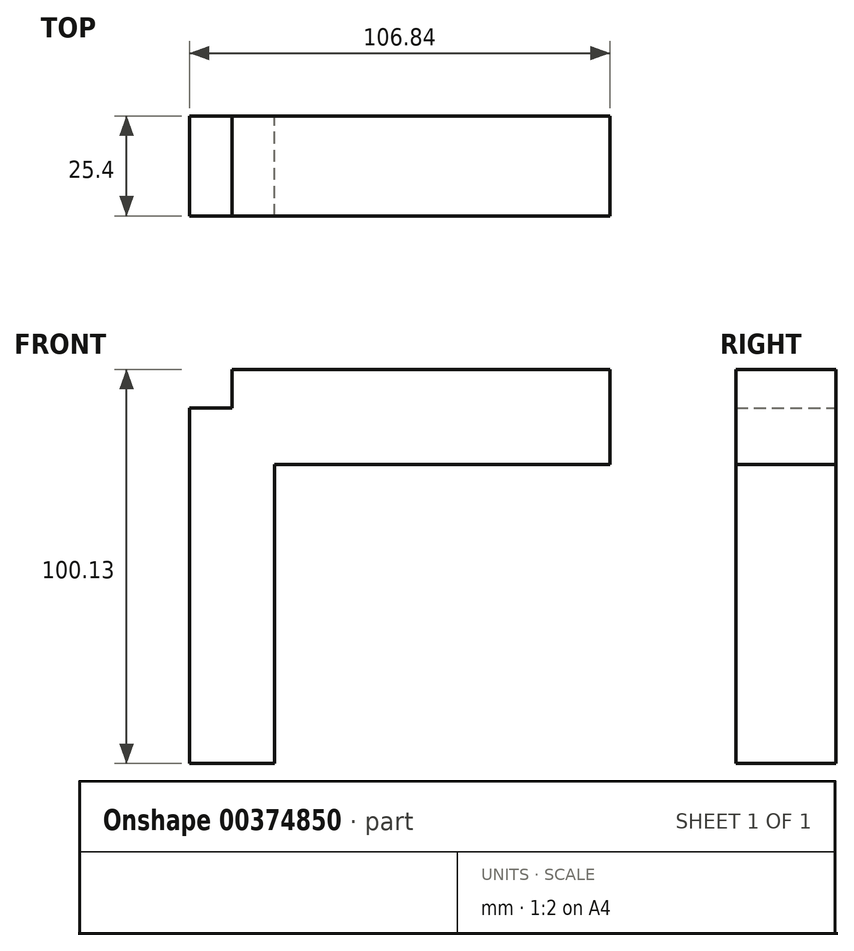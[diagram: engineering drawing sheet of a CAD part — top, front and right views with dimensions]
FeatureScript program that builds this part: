
annotation { "Feature Type Name" : "Feature", "Feature Type Description" : "" }
export const myFeature = defineFeature(function(context is Context, id is Id, definition is map)
    precondition{}
    {
        {
            var Q0;
            Q0=qCreatedBy(makeId("Front.planeOp"),FACE);
            var sketch = newSketch(context, id + "F0", { "sketchPlane" : qUnion([Q0])});
            skLineSegment(sketch, "E0.bottom", {"start": v(21.67, 0) * mm, "end": v(75.4, 0) * mm});
            skLineSegment(sketch, "E0.top", {"start": v(21.67, 24.12) * mm, "end": v(75.4, 24.12) * mm});
            skLineSegment(sketch, "E0.left", {"start": v(0, 0) * mm, "end": v(0, 14.35) * mm});
            skLineSegment(sketch, "E1.bottom", {"start": v(10.84, 24.12) * mm, "end": v(21.67, 24.12) * mm});
            skLineSegment(sketch, "E1.top", {"start": v(0, -76.01) * mm, "end": v(21.67, -76.01) * mm});
            skLineSegment(sketch, "E1.left", {"start": v(0, 14.35) * mm, "end": v(0, -76.01) * mm});
            skLineSegment(sketch, "E1.right", {"start": v(21.67, 0) * mm, "end": v(21.67, -76.01) * mm});
            skLineSegment(sketch, "E2.bottom", {"start": v(43.96, 24.12) * mm, "end": v(69, 24.12) * mm});
            skLineSegment(sketch, "E3.bottom", {"start": v(10.84, 24.12) * mm, "end": v(106.84, 24.12) * mm});
            skLineSegment(sketch, "E3.top", {"start": v(21.67, 0) * mm, "end": v(106.84, 0) * mm});
            skLineSegment(sketch, "E3.left", {"start": v(0, 14.35) * mm, "end": v(0, 0) * mm});
            skLineSegment(sketch, "E3.right", {"start": v(106.84, 24.12) * mm, "end": v(106.84, 0) * mm});
            skLineSegment(sketch, "E4.top", {"start": v(10.84, 14.35) * mm, "end": v(0, 14.35) * mm});
            skLineSegment(sketch, "E4.left", {"start": v(10.84, 24.12) * mm, "end": v(10.84, 14.35) * mm});
            skPoint(sketch, "E4.middle", {"position": v(0, 24.12) * mm});
            skPoint(sketch, "E4.cornerSnap0", {"position": v(10.84, 24.12) * mm});
            skPoint(sketch, "E4.right.start.orphan", {"position": v(-10.84, 33.88) * mm});
            skPoint(sketch, "E5.orphan", {"position": v(-10.84, 14.35) * mm});
            skPoint(sketch, "E6.orphan", {"position": v(10.84, 33.88) * mm});
            skSolve(sketch);
        }
        {
            var Q0;
            Q0 = qSketchRegion(id + "F0", true);
            extrude(context, id + "F1", {"entities" : qUnion([Q0]), "depth" : 25.4 * mm});
        }
    });
